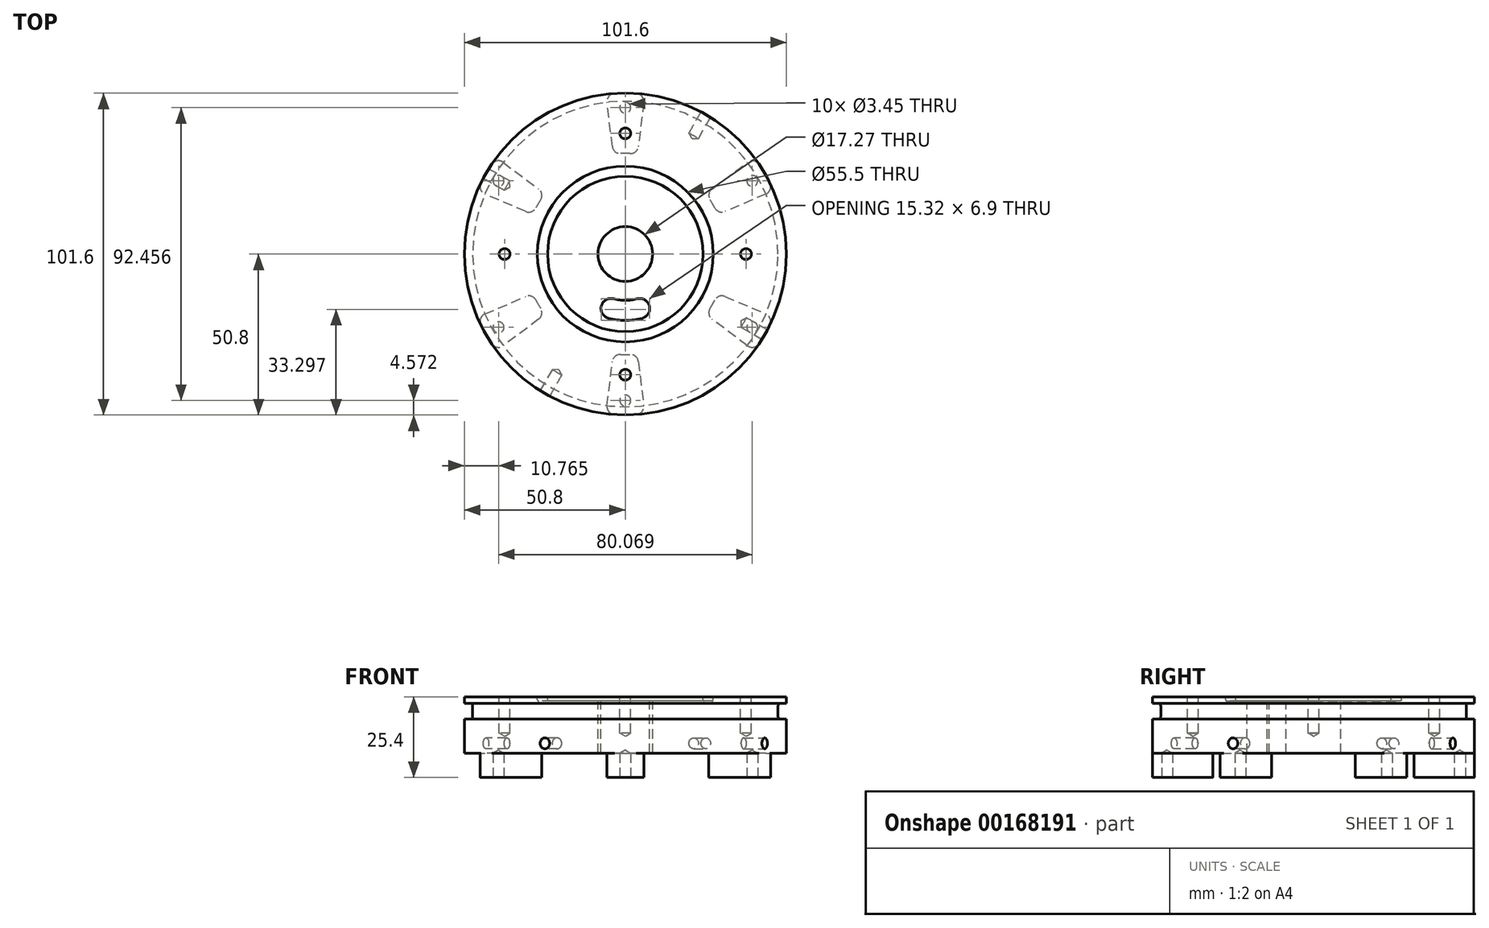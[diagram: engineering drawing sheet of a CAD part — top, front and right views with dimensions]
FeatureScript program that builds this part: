
annotation { "Feature Type Name" : "Feature", "Feature Type Description" : "" }
export const myFeature = defineFeature(function(context is Context, id is Id, definition is map)
    precondition{}
    {
        {
            var Q0;
            Q0=qCreatedBy(makeId("Top.planeOp"),FACE);
            var sketch = newSketch(context, id + "F0", { "sketchPlane" : qUnion([Q0])});
            skCircle(sketch, "E0", {"center": v(0, 0) * mm, "radius": 50.8 * mm});
            skSolve(sketch);
        }
        {
            var Q0;
            Q0=makeQuery(id+"F0.imprint","IMPRINT",FACE,{"disambiguationData":[TD([[makeQuery(id+"F0.imprint","IMPRINT",EDGE,{"derivedFrom":sQuery(id+"F0.wireOp",EDGE,"E0")}),1.0]])]});
            extrude(context, id + "F1", {"entities" : qUnion([Q0]), "depth" : 17.78 * mm});
        }
        {
            var Q0;
            Q0=makeQuery(id+"FNZgXB3MDCEPfWC_1.boolean.opBoolean","SPLIT",FACE,{"disambiguationData":[TD([makeQuery(id+"FNZgXB3MDCEPfWC_1.opExtrude","SWEPT_FACE",FACE,{"disambiguationData":[OSD([sQuery(id+"FiLk9hSRQ8Dv81E_1.wireOp",EDGE,"Xvq2NHEn-EDZK-GzOR-rNrk-moL4fFsD4KvI")])]})])],"derivedFrom":makeQuery(id+"F1.opExtrude","CAP_FACE",FACE,{"disambiguationData":[OSD([sQuery(id+"F0.wireOp",EDGE,"E0")])],"isStart":false})});
            var sketch = newSketch(context, id + "F2", { "sketchPlane" : qUnion([Q0])});
            skCircle(sketch, "E1", {"center": v(0, 0) * mm, "radius": 8.64 * mm});
            skSolve(sketch);
        }
        {
            var Q0;
            Q0=qSketchRegion(id+"F2",true);
            extrude(context, id + "F3", {"entities" : qUnion([Q0]), "operationType" : NewBodyOperationType.REMOVE, "endBound" : BoundingType.THROUGH_ALL, "oppositeDirection" : true, "depth" : 25.4 * mm});
        }
        {
            var Q0;
            Q0=makeQuery(id+"F1.opExtrude","CAP_FACE",FACE,{"disambiguationData":[OSD([sQuery(id+"F0.wireOp",EDGE,"E0")])],"isStart":true});
            var sketch = newSketch(context, id + "F4", { "sketchPlane" : qUnion([Q0])});
            skArc(sketch, "E2", {"start": v(-6.1, -50.43) * mm, "mid": v(0, -50.8) * mm, "end": v(6.1, -50.43) * mm});
            skArc(sketch, "E3", {"start": v(-3.81, -31.52) * mm, "mid": v(0, -31.75) * mm, "end": v(3.8, -31.52) * mm});
            skLineSegment(sketch, "E4", {"start": v(0, 0) * mm, "end": v(3.81, -31.52) * mm, "construction": true});
            skLineSegment(sketch, "E5", {"start": v(6.1, -50.43) * mm, "end": v(3.8, -31.52) * mm});
            skLineSegment(sketch, "E6", {"start": v(-3.8, -31.52) * mm, "end": v(-6.1, -50.43) * mm});
            skLineSegment(sketch, "E7", {"start": v(-3.81, -31.52) * mm, "end": v(3.81, -31.52) * mm, "construction": true});
            skPoint(sketch, "E8", {"position": v(0, -31.52) * mm});
            skLineSegment(sketch, "E9", {"start": v(0, 0) * mm, "end": v(-3.81, -31.52) * mm, "construction": true});
            skSolve(sketch);
        }
        {
            var Q0;
            Q0=qSketchRegion(id+"F4",true);
            extrude(context, id + "F5", {"entities" : qUnion([Q0]), "operationType" : NewBodyOperationType.ADD, "depth" : 7.62 * mm});
        }
        {
            var Q0;
            Q0=makeQuery(id+"F5.opExtrude","SWEPT_EDGE",EDGE,{"disambiguationData":[OSD([sQuery(id+"F0.wireOp",EDGE,"E0"),sQuery(id+"F4.wireOp",EDGE,"E2"),sQuery(id+"F4.wireOp",EDGE,"E5")])]});
            var Q1;
            Q1=makeQuery(id+"F5.opExtrude","SWEPT_EDGE",EDGE,{"disambiguationData":[OSD([sQuery(id+"F4.wireOp",EDGE,"E3"),sQuery(id+"F4.wireOp",EDGE,"E5")])]});
            var Q2;
            Q2=makeQuery(id+"F5.opExtrude","SWEPT_EDGE",EDGE,{"disambiguationData":[OSD([sQuery(id+"F0.wireOp",EDGE,"E0"),sQuery(id+"F4.wireOp",EDGE,"E2"),sQuery(id+"F4.wireOp",EDGE,"sxsrdx0H-xiQs-OsdF-6Z6r-2XBd8uqwUAgb")])]});
            var Q3;
            Q3=makeQuery(id+"F5.opExtrude","SWEPT_EDGE",EDGE,{"disambiguationData":[OSD([sQuery(id+"F4.wireOp",EDGE,"E3"),sQuery(id+"F4.wireOp",EDGE,"sxsrdx0H-xiQs-OsdF-6Z6r-2XBd8uqwUAgb")])]});
            fillet(context, id + "F6", {"entities" : qUnion([Q0, Q1, Q2, Q3]), "radius" : 2.54 * mm, "tangentPropagation" : true, "allowEdgeOverflow" : false});
        }
        {
            var Q0;
            Q0=makeQuery(id+"F5.opExtrude","CAP_FACE",FACE,{"disambiguationData":[OSD([sQuery(id+"F4.wireOp",EDGE,"E2"),sQuery(id+"F4.wireOp",EDGE,"E3"),sQuery(id+"F4.wireOp",EDGE,"E5"),sQuery(id+"F4.wireOp",EDGE,"sxsrdx0H-xiQs-OsdF-6Z6r-2XBd8uqwUAgb")])],"isStart":false});
            var sketch = newSketch(context, id + "F7", { "sketchPlane" : qUnion([Q0])});
            skLineSegment(sketch, "E10", {"start": v(0, 0) * mm, "end": v(0, 0) * mm});
            skLineSegment(sketch, "E11", {"start": v(0, 0) * mm, "end": v(0, -50.68) * mm, "construction": true});
            skPoint(sketch, "E12.3.0", {"position": v(0, -46.23) * mm});
            skPoint(sketch, "E12.center", {"position": v(0, 0) * mm});
            skPoint(sketch, "E13.1.0", {"position": v(40.03, -23.11) * mm});
            skPoint(sketch, "E13.2.0", {"position": v(40.03, 23.11) * mm});
            skPoint(sketch, "E14.0.3.0", {"position": v(0, 46.23) * mm});
            skPoint(sketch, "E14.0.4.0", {"position": v(-40.03, 23.11) * mm});
            skPoint(sketch, "E14.0.5.0", {"position": v(-40.03, -23.11) * mm});
            skSolve(sketch);
        }
        {
            var Q0;
            Q0=makeQuery(id+"F1.opExtrude","SWEPT_BODY",BODY,{"disambiguationData":[OSD([sQuery(id+"F0.wireOp",EDGE,"E0")])]});
            var Q1;
            Q1=makeQuery(id+"F3.boolean.opBoolean","COPY",FACE,{"derivedFrom":makeQuery(id+"F3.opExtrude","SWEPT_FACE",FACE,{"disambiguationData":[OSD([sQuery(id+"F2.wireOp",EDGE,"E1")])]})});
            circularPattern(context, id + "F8", {"operationType" : NewBodyOperationType.ADD, "entities" : qUnion([Q0]), "axis" : qUnion([Q1]), "angle" : 360 * degree, "instanceCount" : 6, "equalSpace" : true});
        }
        {
            var Q0;
            Q0=sQuery(id+"F7.wireOp",VERTEX,"E12.3.0");
            var Q1;
            Q1=sQuery(id+"F7.wireOp",VERTEX,"E13.1.0");
            var Q2;
            Q2=sQuery(id+"F7.wireOp",VERTEX,"E13.2.0");
            var Q3;
            Q3=sQuery(id+"F7.wireOp",VERTEX,"E14.0.3.0");
            var Q4;
            Q4=sQuery(id+"F7.wireOp",VERTEX,"E14.0.4.0");
            var Q5;
            Q5=sQuery(id+"F7.wireOp",VERTEX,"E14.0.5.0");
            var Q6;
            Q6=makeQuery(id+"F1.opExtrude","SWEPT_BODY",BODY,{"disambiguationData":[OSD([sQuery(id+"F0.wireOp",EDGE,"E0")])]});
            hole(context, id + "F9", {"style" : HoleStyle.SIMPLE, "endStyle" : HoleEndStyle.BLIND, "standardTappedOrClearance" : lookupTablePath({ "standard" : "ANSI", "engagement" : "75%", "pitch" : "32 tpi", "size" : "#8", "type" : "Tapped" }), "standardBlindInLast" : lookupTablePath({ "standard" : "ANSI", "engagement" : "75%", "pitch" : "32 tpi", "size" : "#8", "type" : "Tapped" }), "holeDiameter" : 3.45 * mm, "holeDepth" : 7.62 * mm, "locations" : qUnion([Q0, Q1, Q2, Q3, Q4, Q5]), "scope" : qUnion([Q6]), "majorDiameter" : 4.17 * mm});
        }
        {
            var Q0;
            Q0=makeQuery(id+"FkcieFRIapZdHPD_1.boolean.opBoolean","SPLIT",FACE,{"disambiguationData":[TD([makeQuery(id+"F3.boolean.opBoolean","COPY",FACE,{"derivedFrom":makeQuery(id+"F3.opExtrude","SWEPT_FACE",FACE,{"disambiguationData":[OSD([sQuery(id+"F2.wireOp",EDGE,"E1")])]})})])],"derivedFrom":makeQuery(id+"F1.opExtrude","CAP_FACE",FACE,{"disambiguationData":[OSD([sQuery(id+"F0.wireOp",EDGE,"E0")])],"isStart":false})});
            var sketch = newSketch(context, id + "F10", { "sketchPlane" : qUnion([Q0])});
            skCircle(sketch, "E15", {"center": v(0, 0) * mm, "radius": 26.15 * mm, "construction": true});
            skCircle(sketch, "E16", {"center": v(0, 0) * mm, "radius": 24.55 * mm});
            skCircle(sketch, "E17", {"center": v(0, 0) * mm, "radius": 27.75 * mm});
            skSolve(sketch);
        }
        {
            var Q0;
            Q0=qSketchRegion(id+"F10",true);
            extrude(context, id + "F11", {"entities" : qUnion([Q0]), "operationType" : NewBodyOperationType.REMOVE, "oppositeDirection" : true, "depth" : 1.3 * mm});
        }
        {
            var Q0;
            Q0=makeQuery(id+"F11.boolean.opBoolean","COPY",EDGE,{"derivedFrom":makeQuery(id+"F11.opExtrude","CAP_EDGE",EDGE,{"disambiguationData":[OSD([sQuery(id+"F10.wireOp",EDGE,"E17")])],"isStart":false})});
            var Q1;
            Q1=makeQuery(id+"F11.boolean.opBoolean","COPY",EDGE,{"derivedFrom":makeQuery(id+"F11.opExtrude","CAP_EDGE",EDGE,{"disambiguationData":[OSD([sQuery(id+"F10.wireOp",EDGE,"E16")])],"isStart":false})});
            fillet(context, id + "F12", {"entities" : qUnion([Q0, Q1]), "radius" : 0.4 * mm, "tangentPropagation" : true, "allowEdgeOverflow" : false});
        }
        {
            var Q0;
            {var subQ0=makeQuery(id+"F3.boolean.opBoolean","COPY",FACE,{"derivedFrom":makeQuery(id+"F3.opExtrude","SWEPT_FACE",FACE,{"disambiguationData":[OSD([sQuery(id+"F2.wireOp",EDGE,"E1")])]})});Q0=makeQuery(id+"F11.boolean.opBoolean","SPLIT",FACE,{"disambiguationData":[TD([subQ0])],"derivedFrom":makeQuery(id+"FkcieFRIapZdHPD_1.boolean.opBoolean","SPLIT",FACE,{"disambiguationData":[TD([subQ0])],"derivedFrom":makeQuery(id+"F1.opExtrude","CAP_FACE",FACE,{"disambiguationData":[OSD([sQuery(id+"F0.wireOp",EDGE,"E0")])],"isStart":false})})});}
            var sketch = newSketch(context, id + "F13", { "sketchPlane" : qUnion([Q0])});
            skLineSegment(sketch, "E18", {"start": v(0, 0) * mm, "end": v(6.17, -13.24) * mm, "construction": true});
            skArc(sketch, "E19", {"start": v(6.17, -13.24) * mm, "mid": v(0, -14.6) * mm, "end": v(-6.17, -13.24) * mm});
            skArc(sketch, "E20", {"start": v(8.86, -19) * mm, "mid": v(0, -20.95) * mm, "end": v(-8.86, -19) * mm});
            skLineSegment(sketch, "E21", {"start": v(-8.86, -19) * mm, "end": v(-6.17, -13.24) * mm});
            skLineSegment(sketch, "E22", {"start": v(0, 0) * mm, "end": v(-6.17, -13.24) * mm, "construction": true});
            skLineSegment(sketch, "E23", {"start": v(8.86, -19) * mm, "end": v(6.17, -13.24) * mm});
            skLineSegment(sketch, "E24", {"start": v(0, -14.6) * mm, "end": v(0, 0) * mm, "construction": true});
            skPoint(sketch, "E25", {"position": v(-7.51, -16.11) * mm});
            skSolve(sketch);
        }
        {
            var Q0;
            Q0=qSketchRegion(id+"F13",true);
            extrude(context, id + "F14", {"entities" : qUnion([Q0]), "operationType" : NewBodyOperationType.REMOVE, "endBound" : BoundingType.THROUGH_ALL, "oppositeDirection" : true, "depth" : 25.4 * mm});
        }
        {
            var Q0;
            Q0=makeQuery(id+"F14.boolean.opBoolean","COPY",EDGE,{"derivedFrom":makeQuery(id+"F14.opExtrude","SWEPT_EDGE",EDGE,{"disambiguationData":[OSD([sQuery(id+"F13.wireOp",EDGE,"E19"),sQuery(id+"F13.wireOp",EDGE,"E21")])]})});
            var Q1;
            Q1=makeQuery(id+"F14.boolean.opBoolean","COPY",EDGE,{"derivedFrom":makeQuery(id+"F14.opExtrude","SWEPT_EDGE",EDGE,{"disambiguationData":[OSD([sQuery(id+"F13.wireOp",EDGE,"E20"),sQuery(id+"F13.wireOp",EDGE,"E21")])]})});
            var Q2;
            Q2=makeQuery(id+"F14.boolean.opBoolean","COPY",EDGE,{"derivedFrom":makeQuery(id+"F14.opExtrude","SWEPT_EDGE",EDGE,{"disambiguationData":[OSD([sQuery(id+"F13.wireOp",EDGE,"E19"),sQuery(id+"F13.wireOp",EDGE,"nJm0js4g-YAOA-XNub-Ppl5-B8IrQimasCNu")])]})});
            var Q3;
            Q3=makeQuery(id+"F14.boolean.opBoolean","COPY",EDGE,{"derivedFrom":makeQuery(id+"F14.opExtrude","SWEPT_EDGE",EDGE,{"disambiguationData":[OSD([sQuery(id+"F13.wireOp",EDGE,"E20"),sQuery(id+"F13.wireOp",EDGE,"nJm0js4g-YAOA-XNub-Ppl5-B8IrQimasCNu")])]})});
            fillet(context, id + "F15", {"entities" : qUnion([Q0, Q1, Q2, Q3]), "radius" : 3.17 * mm, "tangentPropagation" : true, "allowEdgeOverflow" : false});
        }
        {
            var Q0;
            {var subQ0=makeQuery(id+"F3.boolean.opBoolean","COPY",FACE,{"derivedFrom":makeQuery(id+"F3.opExtrude","SWEPT_FACE",FACE,{"disambiguationData":[OSD([sQuery(id+"F2.wireOp",EDGE,"E1")])]})});Q0=makeQuery(id+"F11.boolean.opBoolean","SPLIT",FACE,{"disambiguationData":[TD([subQ0])],"derivedFrom":makeQuery(id+"FkcieFRIapZdHPD_1.boolean.opBoolean","SPLIT",FACE,{"disambiguationData":[TD([subQ0])],"derivedFrom":makeQuery(id+"F1.opExtrude","CAP_FACE",FACE,{"disambiguationData":[OSD([sQuery(id+"F0.wireOp",EDGE,"E0")])],"isStart":false})})});}
            var sketch = newSketch(context, id + "F16", { "sketchPlane" : qUnion([Q0])});
            skCircle(sketch, "E26", {"center": v(0, 0) * mm, "radius": 38.1 * mm, "construction": true});
            skLineSegment(sketch, "E27", {"start": v(0, 0) * mm, "end": v(0, -38.1) * mm, "construction": true});
            skPoint(sketch, "E28", {"position": v(0, -38.1) * mm});
            skPoint(sketch, "E29", {"position": v(-38.1, 0) * mm});
            skPoint(sketch, "E30", {"position": v(38.1, 0) * mm});
            skPoint(sketch, "E31", {"position": v(0, 38.1) * mm});
            skSolve(sketch);
        }
        {
            var Q0;
            Q0=sQuery(id+"F16.wireOp",VERTEX,"E29");
            var Q1;
            Q1=sQuery(id+"F16.wireOp",VERTEX,"E31");
            var Q2;
            Q2=sQuery(id+"F16.wireOp",VERTEX,"E30");
            var Q3;
            Q3=sQuery(id+"F16.wireOp",VERTEX,"E28");
            var Q4;
            Q4=makeQuery(id+"F1.opExtrude","SWEPT_BODY",BODY,{"disambiguationData":[OSD([sQuery(id+"F0.wireOp",EDGE,"E0")])]});
            hole(context, id + "F17", {"style" : HoleStyle.SIMPLE, "endStyle" : HoleEndStyle.BLIND, "standardTappedOrClearance" : lookupTablePath({ "standard" : "ANSI", "engagement" : "75%", "pitch" : "32 tpi", "size" : "#8", "type" : "Tapped" }), "standardBlindInLast" : lookupTablePath({ "standard" : "ANSI", "engagement" : "75%", "pitch" : "32 tpi", "size" : "#8", "type" : "Tapped" }), "holeDiameter" : 3.45 * mm, "holeDepth" : 11.43 * mm, "locations" : qUnion([Q0, Q1, Q2, Q3]), "scope" : qUnion([Q4]), "majorDiameter" : 4.17 * mm});
        }
        {
            var Q0;
            Q0=makeQuery(id+"F11.boolean.opBoolean","SPLIT",FACE,{"disambiguationData":[TD([makeQuery(id+"F3.boolean.opBoolean","COPY",FACE,{"derivedFrom":makeQuery(id+"F3.opExtrude","SWEPT_FACE",FACE,{"disambiguationData":[OSD([sQuery(id+"F2.wireOp",EDGE,"E1")])]})})])],"derivedFrom":makeQuery(id+"F1.opExtrude","CAP_FACE",FACE,{"disambiguationData":[OSD([sQuery(id+"F0.wireOp",EDGE,"E0")])],"isStart":false})});
            cPlane(context, id + "F18", {"entities" : qUnion([Q0]), "cplaneType" : CPlaneType.OFFSET, "offset" : 2.03 * mm, "oppositeDirection" : true, "width" : 152.4 * mm, "height" : 152.4 * mm});
        }
        {
            var Q0;
            Q0=qCreatedBy(id+"F18.planeOp",FACE);
            var sketch = newSketch(context, id + "F19", { "sketchPlane" : qUnion([Q0])});
            skCircle(sketch, "E32", {"center": v(0, 0) * mm, "radius": 48.2 * mm});
            skCircle(sketch, "E33.0", {"center": v(0, 0) * mm, "radius": 50.8 * mm});
            skSolve(sketch);
        }
        {
            var Q0;
            Q0=qSketchRegion(id+"F19",true);
            extrude(context, id + "F20", {"entities" : qUnion([Q0]), "operationType" : NewBodyOperationType.REMOVE, "oppositeDirection" : true, "depth" : 5 * mm});
        }
        {
            var Q0;
            Q0=makeQuery(id+"F20.boolean.opBoolean","COPY",EDGE,{"derivedFrom":makeQuery(id+"F20.opExtrude","CAP_EDGE",EDGE,{"disambiguationData":[OSD([sQuery(id+"F19.wireOp",EDGE,"E32")])],"isStart":false})});
            var Q1;
            Q1=makeQuery(id+"F20.boolean.opBoolean","COPY",EDGE,{"derivedFrom":makeQuery(id+"F20.opExtrude","CAP_EDGE",EDGE,{"disambiguationData":[OSD([sQuery(id+"F19.wireOp",EDGE,"E32")])],"isStart":true})});
            fillet(context, id + "F21", {"entities" : qUnion([Q0, Q1]), "radius" : 0.76 * mm, "tangentPropagation" : true, "allowEdgeOverflow" : false});
        }
        {
            var Q0;
            {var subQ1=sQuery(id+"F0.wireOp",EDGE,"E0");var subQ2=makeQuery(id+"F1.opExtrude","SWEPT_FACE",FACE,{"disambiguationData":[OSD([subQ1])]});Q0=makeQuery(id+"FkcieFRIapZdHPD_1.boolean.opBoolean","SPLIT",FACE,{"disambiguationData":[TD([subQ2])],"derivedFrom":makeQuery(id+"F1.opExtrude","CAP_FACE",FACE,{"disambiguationData":[OSD([subQ1])],"isStart":false})});}
            var sketch = newSketch(context, id + "F22", { "sketchPlane" : qUnion([Q0])});
            skCircle(sketch, "E34.0", {"center": v(0, 0) * mm, "radius": 50.8 * mm, "construction": true});
            skPoint(sketch, "E35", {"position": v(-25.4, -44) * mm});
            skLineSegment(sketch, "E36", {"start": v(0, -50.8) * mm, "end": v(0, 0) * mm, "construction": true});
            skLineSegment(sketch, "E37", {"start": v(0, 0) * mm, "end": v(-17.96, -31.1) * mm, "construction": true});
            skLineSegment(sketch, "E38", {"start": v(-17.96, -31.1) * mm, "end": v(-25.4, -44) * mm, "construction": true});
            skLineSegment(sketch, "E39", {"start": v(0, 0) * mm, "end": v(25.4, 44) * mm, "construction": true});
            skLineSegment(sketch, "E40", {"start": v(25.4, 44) * mm, "end": v(0, 0) * mm, "construction": true});
            skLineSegment(sketch, "E41", {"start": v(44, -25.4) * mm, "end": v(0, 0) * mm, "construction": true});
            skLineSegment(sketch, "E42", {"start": v(0, 0) * mm, "end": v(-44, 25.4) * mm, "construction": true});
            skPoint(sketch, "E43", {"position": v(25.4, 44) * mm});
            skPoint(sketch, "E44", {"position": v(44, -25.4) * mm});
            skPoint(sketch, "E45", {"position": v(-44, 25.4) * mm});
            skSolve(sketch);
        }
        {
            var Q0;
            Q0=qCreatedBy(makeId("Front.planeOp"),FACE);
            var sketch = newSketch(context, id + "F23", { "sketchPlane" : qUnion([Q0])});
            skLineSegment(sketch, "E46", {"start": v(0, 0) * mm, "end": v(0, 38.57) * mm, "construction": true});
            skSolve(sketch);
        }
        {
            var Q0;
            Q0=sQuery(id+"F23.wireOp",EDGE,"E46");
            cPlane(context, id + "F24", {"entities" : qUnion([Q0]), "cplaneType" : CPlaneType.LINE_ANGLE, "offset" : 25.4 * mm, "angle" : 60 * degree, "width" : 152.4 * mm, "height" : 152.4 * mm});
        }
        {
            var Q0;
            Q0=sQuery(id+"F22.wireOp",VERTEX,"E35");
            var Q1;
            Q1=qCreatedBy(id+"F24.planeOp",FACE);
            cPlane(context, id + "F25", {"entities" : qUnion([Q0, Q1]), "cplaneType" : CPlaneType.PLANE_POINT, "offset" : 25.4 * mm, "width" : 152.4 * mm, "height" : 152.4 * mm});
        }
        {
            var Q0;
            Q0=qCreatedBy(id+"F25.planeOp",FACE);
            var Q1;
            Q1=sQuery(id+"F22.wireOp",VERTEX,"E43");
            cPlane(context, id + "F26", {"entities" : qUnion([Q0, Q1]), "cplaneType" : CPlaneType.PLANE_POINT, "offset" : 25.4 * mm, "width" : 152.4 * mm, "height" : 152.4 * mm});
        }
        {
            var Q0;
            Q0=sQuery(id+"F23.wireOp",EDGE,"E46");
            cPlane(context, id + "F27", {"entities" : qUnion([Q0]), "cplaneType" : CPlaneType.LINE_ANGLE, "offset" : 25.4 * mm, "angle" : 150 * degree, "width" : 152.4 * mm, "height" : 152.4 * mm});
        }
        {
            var Q0;
            Q0=sQuery(id+"F22.wireOp",VERTEX,"E45");
            var Q1;
            Q1=qCreatedBy(id+"F27.planeOp",FACE);
            cPlane(context, id + "F28", {"entities" : qUnion([Q0, Q1]), "cplaneType" : CPlaneType.PLANE_POINT, "offset" : 25.4 * mm, "width" : 152.4 * mm, "height" : 152.4 * mm});
        }
        {
            var Q0;
            Q0=qCreatedBy(id+"F27.planeOp",FACE);
            var Q1;
            Q1=sQuery(id+"F22.wireOp",VERTEX,"E44");
            cPlane(context, id + "F29", {"entities" : qUnion([Q0, Q1]), "cplaneType" : CPlaneType.PLANE_POINT, "offset" : 25.4 * mm, "width" : 152.4 * mm, "height" : 152.4 * mm});
        }
        {
            var Q0;
            Q0=qCreatedBy(id+"F25.planeOp",FACE);
            var sketch = newSketch(context, id + "F30", { "sketchPlane" : qUnion([Q0])});
            skLineSegment(sketch, "E47", {"start": v(0, 0) * mm, "end": v(0, 3.12) * mm, "construction": true});
            skPoint(sketch, "E48", {"position": v(0, 3.12) * mm});
            skSolve(sketch);
        }
        {
            var Q0;
            Q0=qCreatedBy(id+"F26.planeOp",FACE);
            var sketch = newSketch(context, id + "F31", { "sketchPlane" : qUnion([Q0])});
            skPoint(sketch, "E49", {"position": v(0, 3.12) * mm});
            skLineSegment(sketch, "E50.0", {"start": v(0, 0) * mm, "end": v(0, 3.12) * mm, "construction": true});
            skSolve(sketch);
        }
        {
            var Q0;
            Q0=qCreatedBy(id+"F28.planeOp",FACE);
            var sketch = newSketch(context, id + "F32", { "sketchPlane" : qUnion([Q0])});
            skLineSegment(sketch, "E51", {"start": v(0, 0) * mm, "end": v(0, 3.12) * mm, "construction": true});
            skLineSegment(sketch, "E52.0", {"start": v(-50.8, 0) * mm, "end": v(-50.8, 3.12) * mm, "construction": true});
            skPoint(sketch, "E53", {"position": v(0, 3.12) * mm});
            skLineSegment(sketch, "E54", {"start": v(-50.8, 3.12) * mm, "end": v(0, 3.12) * mm, "construction": true});
            skSolve(sketch);
        }
        {
            var Q0;
            Q0=qCreatedBy(id+"F29.planeOp",FACE);
            var sketch = newSketch(context, id + "F33", { "sketchPlane" : qUnion([Q0])});
            skLineSegment(sketch, "E55.0", {"start": v(0, 0) * mm, "end": v(0, 3.12) * mm, "construction": true});
            skPoint(sketch, "E56", {"position": v(0, 3.12) * mm});
            skSolve(sketch);
        }
        {
            var Q0;
            Q0=sQuery(id+"F33.wireOp",VERTEX,"E56");
            var Q1;
            Q1=makeQuery(id+"F1.opExtrude","SWEPT_BODY",BODY,{"disambiguationData":[OSD([sQuery(id+"F0.wireOp",EDGE,"E0")])]});
            hole(context, id + "F34", {"style" : HoleStyle.SIMPLE, "endStyle" : HoleEndStyle.BLIND, "oppositeDirection" : true, "standardTappedOrClearance" : lookupTablePath({ "standard" : "ANSI", "engagement" : "75%", "pitch" : "32 tpi", "size" : "#8", "type" : "Tapped" }), "standardBlindInLast" : lookupTablePath({ "standard" : "ANSI", "engagement" : "75%", "pitch" : "32 tpi", "size" : "#8", "type" : "Tapped" }), "holeDiameter" : 3.45 * mm, "holeDepth" : 7.62 * mm, "locations" : qUnion([Q0]), "scope" : qUnion([Q1]), "majorDiameter" : 4.17 * mm});
        }
        {
            var Q0;
            Q0=sQuery(id+"F32.wireOp",VERTEX,"E53");
            var Q1;
            Q1=makeQuery(id+"F1.opExtrude","SWEPT_BODY",BODY,{"disambiguationData":[OSD([sQuery(id+"F0.wireOp",EDGE,"E0")])]});
            hole(context, id + "F35", {"style" : HoleStyle.SIMPLE, "endStyle" : HoleEndStyle.BLIND, "standardTappedOrClearance" : lookupTablePath({ "standard" : "ANSI", "engagement" : "75%", "pitch" : "32 tpi", "size" : "#8", "type" : "Tapped" }), "standardBlindInLast" : lookupTablePath({ "standard" : "ANSI", "engagement" : "75%", "pitch" : "32 tpi", "size" : "#8", "type" : "Tapped" }), "holeDiameter" : 3.45 * mm, "holeDepth" : 7.62 * mm, "locations" : qUnion([Q0]), "scope" : qUnion([Q1]), "majorDiameter" : 4.17 * mm});
        }
        {
            var Q0;
            Q0=sQuery(id+"F30.wireOp",VERTEX,"E48");
            var Q1;
            Q1=makeQuery(id+"F1.opExtrude","SWEPT_BODY",BODY,{"disambiguationData":[OSD([sQuery(id+"F0.wireOp",EDGE,"E0")])]});
            hole(context, id + "F36", {"style" : HoleStyle.SIMPLE, "endStyle" : HoleEndStyle.BLIND, "oppositeDirection" : true, "standardTappedOrClearance" : lookupTablePath({ "standard" : "ANSI", "engagement" : "75%", "pitch" : "32 tpi", "size" : "#8", "type" : "Tapped" }), "standardBlindInLast" : lookupTablePath({ "standard" : "ANSI", "engagement" : "75%", "pitch" : "32 tpi", "size" : "#8", "type" : "Tapped" }), "holeDiameter" : 3.45 * mm, "holeDepth" : 7.62 * mm, "locations" : qUnion([Q0]), "scope" : qUnion([Q1]), "majorDiameter" : 4.17 * mm});
        }
        {
            var Q0;
            Q0=sQuery(id+"F31.wireOp",VERTEX,"E49");
            var Q1;
            Q1=makeQuery(id+"F1.opExtrude","SWEPT_BODY",BODY,{"disambiguationData":[OSD([sQuery(id+"F0.wireOp",EDGE,"E0")])]});
            hole(context, id + "F37", {"style" : HoleStyle.SIMPLE, "endStyle" : HoleEndStyle.BLIND, "standardTappedOrClearance" : lookupTablePath({ "standard" : "ANSI", "engagement" : "75%", "pitch" : "32 tpi", "size" : "#8", "type" : "Tapped" }), "standardBlindInLast" : lookupTablePath({ "standard" : "ANSI", "engagement" : "75%", "pitch" : "32 tpi", "size" : "#8", "type" : "Tapped" }), "holeDiameter" : 3.45 * mm, "holeDepth" : 7.62 * mm, "locations" : qUnion([Q0]), "scope" : qUnion([Q1]), "majorDiameter" : 4.17 * mm});
        }
    });
